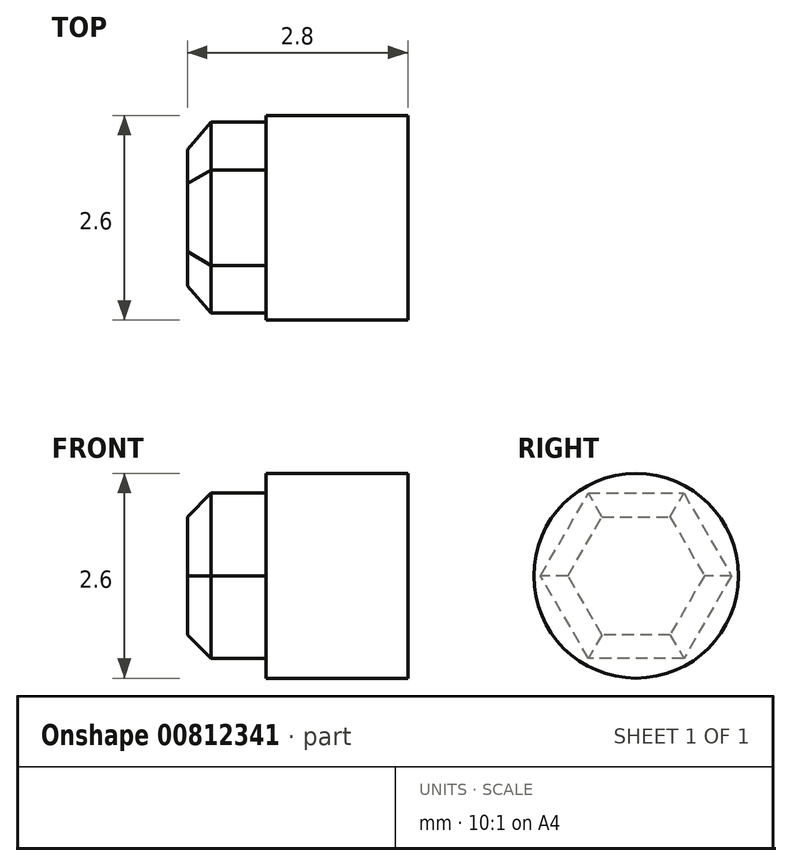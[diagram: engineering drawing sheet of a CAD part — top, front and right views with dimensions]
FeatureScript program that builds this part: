
annotation { "Feature Type Name" : "Feature", "Feature Type Description" : "" }
export const myFeature = defineFeature(function(context is Context, id is Id, definition is map)
    precondition{}
    {
        {
            var Q0;
            Q0=qCreatedBy(makeId("Right.planeOp"),FACE);
            var sketch = newSketch(context, id + "F0", { "sketchPlane" : qUnion([Q0])});
            skCircle(sketch, "E0", {"center": v(0, 0) * mm, "radius": 1.3 * mm});
            skSolve(sketch);
        }
        {
            var Q0;
            Q0 = qSketchRegion(id + "F0", true);
            extrude(context, id + "F1", {"entities" : qUnion([Q0]), "depth" : 1.8 * mm, "offsetDistance" : 25 * mm});
        }
        {
            var Q0;
            Q0=qCreatedBy(makeId("Right.planeOp"),FACE);
            var sketch = newSketch(context, id + "F2", { "sketchPlane" : qUnion([Q0])});
            skCircle(sketch, "E1.cCircle", {"center": v(0, 0) * mm, "radius": 1.05 * mm, "construction": true});
            skLineSegment(sketch, "E1.0", {"start": v(-0.6, 1.05) * mm, "end": v(0.6, 1.05) * mm});
            skLineSegment(sketch, "E1.1", {"start": v(0.6, 1.05) * mm, "end": v(1.21, 0) * mm});
            skLineSegment(sketch, "E1.2", {"start": v(1.21, 0) * mm, "end": v(0.6, -1.05) * mm});
            skLineSegment(sketch, "E1.3", {"start": v(0.6, -1.05) * mm, "end": v(-0.6, -1.05) * mm});
            skLineSegment(sketch, "E1.4", {"start": v(-0.6, -1.05) * mm, "end": v(-1.21, 0) * mm});
            skLineSegment(sketch, "E1.5", {"start": v(-1.21, 0) * mm, "end": v(-0.6, 1.05) * mm});
            skPoint(sketch, "E1.0.midPoint", {"position": v(0, 1.05) * mm});
            skSolve(sketch);
        }
        {
            var Q0;
            Q0 = qSketchRegion(id + "F2", true);
            extrude(context, id + "F3", {"entities" : qUnion([Q0]), "operationType" : NewBodyOperationType.ADD, "oppositeDirection" : true, "depth" : 1 * mm, "offsetDistance" : 25 * mm});
        }
        {
            var Q0;
            Q0=makeQuery(id+"F3.opExtrude","CAP_FACE",FACE,{"disambiguationData":[OSD([sQuery(id+"F2.wireOp",EDGE,"E1.0"),sQuery(id+"F2.wireOp",EDGE,"E1.1"),sQuery(id+"F2.wireOp",EDGE,"E1.2"),sQuery(id+"F2.wireOp",EDGE,"E1.3"),sQuery(id+"F2.wireOp",EDGE,"E1.4"),sQuery(id+"F2.wireOp",EDGE,"E1.5")])],"isStart":false});
            chamfer(context, id + "F4", {"entities" : qUnion([Q0]), "width" : .3 * mm, "tangentPropagation" : true});
        }
    });
